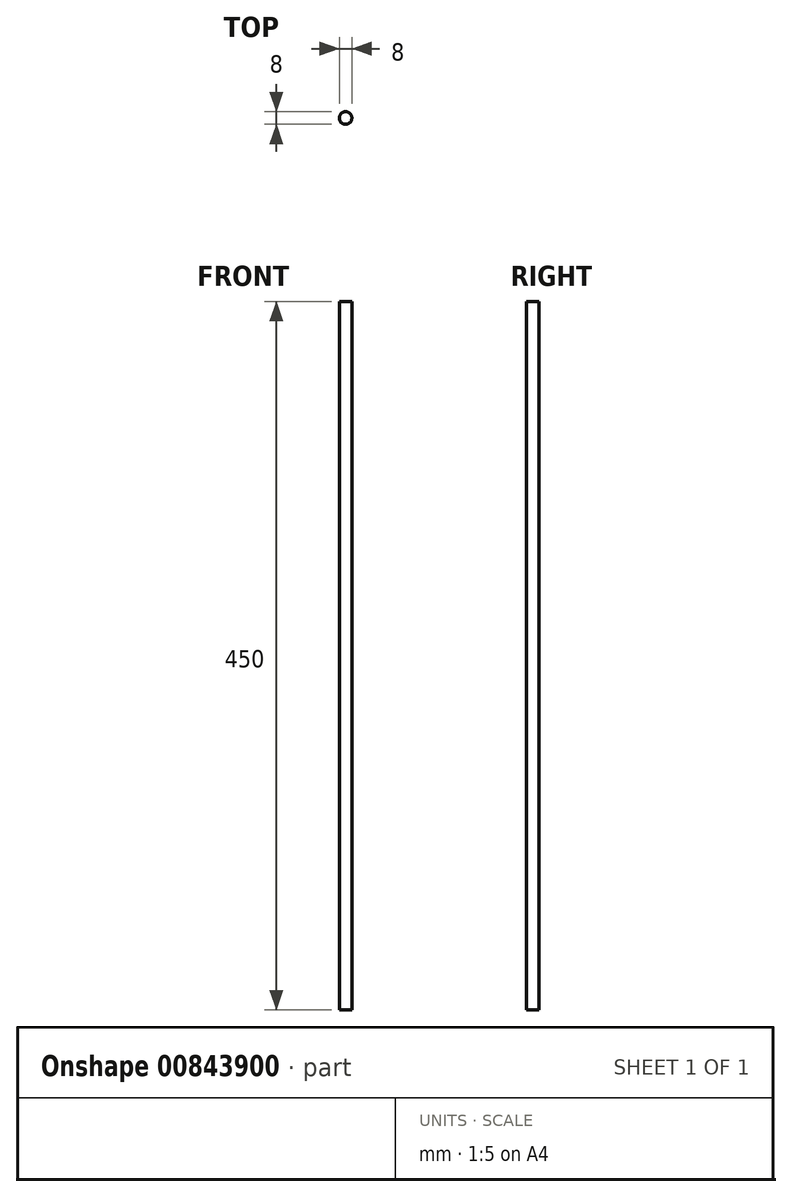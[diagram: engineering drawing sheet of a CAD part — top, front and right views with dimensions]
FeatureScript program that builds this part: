
annotation { "Feature Type Name" : "Feature", "Feature Type Description" : "" }
export const myFeature = defineFeature(function(context is Context, id is Id, definition is map)
    precondition{}
    {
        {
            var Q0;
            Q0=qCreatedBy(makeId("Top.planeOp"),FACE);
            var sketch = newSketch(context, id + "F0", { "sketchPlane" : qUnion([Q0])});
            skCircle(sketch, "E0", {"center": v(0, 0) * mm, "radius": 4 * mm});
            skSolve(sketch);
        }
        {
            var Q0;
            Q0=makeQuery(id+"F0.imprint","IMPRINT",FACE,{"disambiguationData":[TD([[makeQuery(id+"F0.imprint","IMPRINT",EDGE,{"derivedFrom":sQuery(id+"F0.wireOp",EDGE,"E0")}),1.0]])]});
            extrude(context, id + "F1", {"entities" : qUnion([Q0]), "depth" : 450 * mm, "offsetDistance" : 25 * mm});
        }
    });
